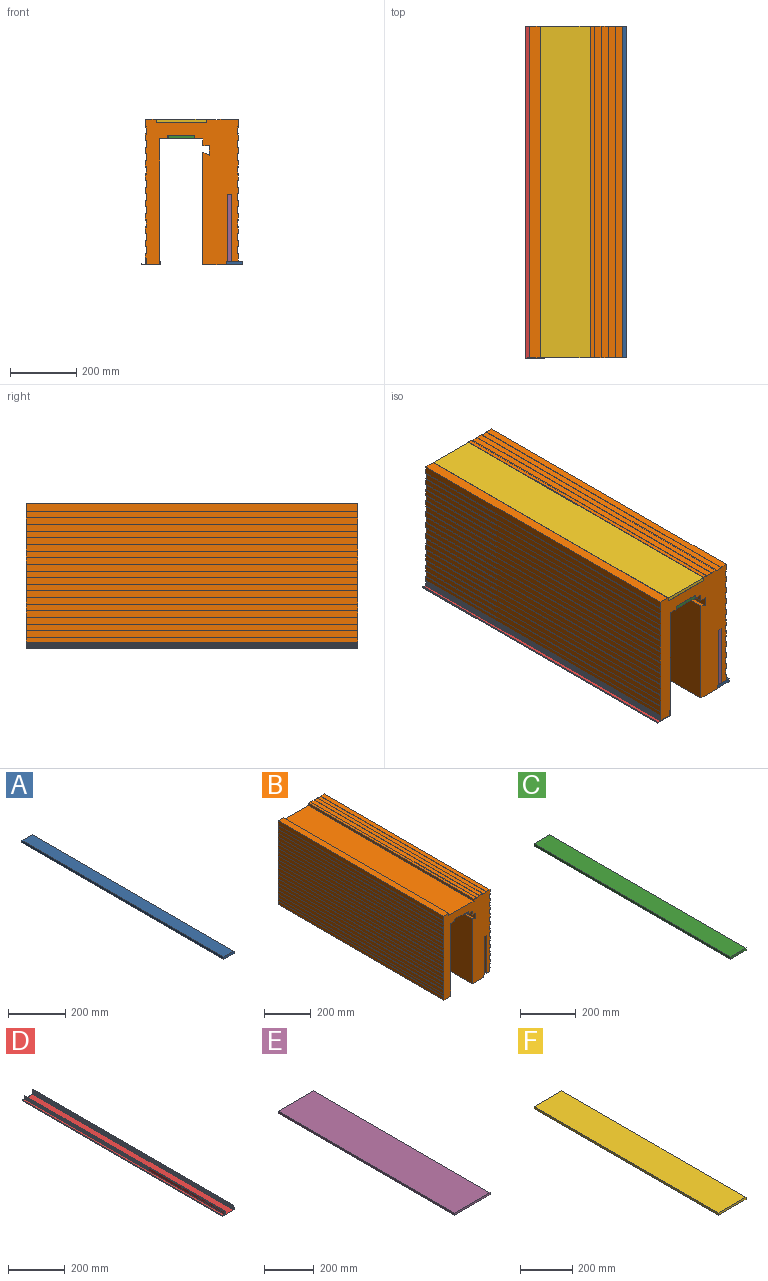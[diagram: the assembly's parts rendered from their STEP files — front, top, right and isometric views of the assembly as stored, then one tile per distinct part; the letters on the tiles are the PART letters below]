
ASSEMBLY  parts=6 mates=5
PART A: 6 faces, bbox 50x1000x10 mm
  f0: plane 1000x10mm, normal (-1,0,0), area 10000mm2, adj f1,f3,f4,f5
  f1: plane 1000x50mm, normal (0,0,-1), area 50000mm2, adj f0,f2,f4,f5
  f2: plane 1000x10mm, normal (1,0,0), area 10000mm2, adj f1,f3,f4,f5
  f3: plane 1000x50mm, normal (0,0,1), area 50000mm2, adj f0,f2,f4,f5
  f4: plane 50x10mm, normal (0,-1,0), area 500mm2, adj f0,f1,f2,f3
  f5: plane 50x10mm, normal (0,1,0), area 500mm2, adj f0,f1,f2,f3
PART B: 120 faces, bbox 280x1000x440 mm
  f0: plane 1000x2mm, normal (0.89,0,-0.45), area 2236.1mm2, adj f1,f117,f118,f119
  f1: plane 1000x20mm, normal (0,0,1), area 20000mm2, adj f0,f2,f118,f119
  f2: plane 1000x2mm, normal (-0.89,0,-0.45), area 2236.1mm2, adj f1,f3,f118,f119
  f3: plane 1000x23mm, normal (0,0,1), area 23000mm2, adj f2,f4,f118,f119
  f4: plane 1000x2mm, normal (0.89,0,-0.45), area 2236.1mm2, adj f3,f5,f118,f119
  f5: plane 1000x13.5mm, normal (0,0,1), area 13500mm2, adj f4,f6,f118,f119
  f6: plane 1000x11.5mm, normal (-1,0,0), area 11500mm2, adj f5,f7,f118,f119
  f7: plane 1000x151mm, normal (0,0,1), area 151000mm2, adj f6,f8,f118,f119
  f8: plane 1000x11.5mm, normal (1,0,0), area 11500mm2, adj f7,f9,f118,f119
  f9: plane 1000x32.4mm, normal (0,0,1), area 32400mm2, adj f8,f10,f118,f119
  f10: plane 1000x25mm, normal (-1,0,0), area 25000mm2, adj f9,f11,f118,f119
  f11: plane 1000x2mm, normal (0.45,0,-0.89), area 2236.1mm2, adj f10,f12,f118,f119
  f12: plane 1000x22mm, normal (-1,0,0), area 22000mm2, adj f11,f13,f118,f119
  f13: plane 1000x2mm, normal (0.45,0,0.89), area 2236.1mm2, adj f12,f14,f118,f119
  f14: plane 1000x20mm, normal (-1,0,0), area 20000mm2, adj f13,f15,f118,f119
  f15: plane 1000x2mm, normal (0.45,0,-0.89), area 2236.1mm2, adj f14,f16,f118,f119
  f16: plane 1000x22mm, normal (-1,0,0), area 22000mm2, adj f15,f17,f118,f119
  f17: plane 1000x2mm, normal (0.45,0,0.89), area 2236.1mm2, adj f16,f18,f118,f119
  f18: plane 1000x20mm, normal (-1,0,0), area 20000mm2, adj f17,f19,f118,f119
  f19: plane 1000x2mm, normal (0.45,0,-0.89), area 2236.1mm2, adj f18,f20,f118,f119
  f20: plane 1000x22mm, normal (-1,0,0), area 22000mm2, adj f19,f21,f118,f119
  f21: plane 1000x2mm, normal (0.45,0,0.89), area 2236.1mm2, adj f20,f22,f118,f119
  f22: plane 1000x20mm, normal (-1,0,0), area 20000mm2, adj f21,f23,f118,f119
  f23: plane 1000x2mm, normal (0.45,0,-0.89), area 2236.1mm2, adj f22,f24,f118,f119
  f24: plane 1000x22mm, normal (-1,0,0), area 22000mm2, adj f23,f25,f118,f119
  f25: plane 1000x2mm, normal (0.45,0,0.89), area 2236.1mm2, adj f24,f26,f118,f119
  f26: plane 1000x20mm, normal (-1,0,0), area 20000mm2, adj f25,f27,f118,f119
  f27: plane 1000x2mm, normal (0.45,0,-0.89), area 2236.1mm2, adj f26,f28,f118,f119
  f28: plane 1000x22mm, normal (-1,0,0), area 22000mm2, adj f27,f29,f118,f119
  f29: plane 1000x2mm, normal (0.45,0,0.89), area 2236.1mm2, adj f28,f30,f118,f119
  f30: plane 1000x20mm, normal (-1,0,0), area 20000mm2, adj f29,f31,f118,f119
  f31: plane 1000x2mm, normal (0.45,0,-0.89), area 2236.1mm2, adj f30,f32,f118,f119
  f32: plane 1000x22mm, normal (-1,0,0), area 22000mm2, adj f31,f33,f118,f119
  f33: plane 1000x2mm, normal (0.45,0,0.89), area 2236.1mm2, adj f32,f34,f118,f119
  f34: plane 1000x20mm, normal (-1,0,0), area 20000mm2, adj f33,f35,f118,f119
  f35: plane 1000x2mm, normal (0.45,0,-0.89), area 2236.1mm2, adj f34,f36,f118,f119
  f36: plane 1000x22mm, normal (-1,0,0), area 22000mm2, adj f35,f37,f118,f119
  f37: plane 1000x2mm, normal (0.45,0,0.89), area 2236.1mm2, adj f36,f38,f118,f119
  f38: plane 1000x20mm, normal (-1,0,0), area 20000mm2, adj f37,f39,f118,f119
  f39: plane 1000x2mm, normal (0.45,0,-0.89), area 2236.1mm2, adj f38,f40,f118,f119
  f40: plane 1000x22mm, normal (-1,0,0), area 22000mm2, adj f39,f41,f118,f119
  f41: plane 1000x2mm, normal (0.45,0,0.89), area 2236.1mm2, adj f40,f42,f118,f119
  f42: plane 1000x20mm, normal (-1,0,0), area 20000mm2, adj f41,f43,f118,f119
  f43: plane 1000x2mm, normal (0.45,0,-0.89), area 2236.1mm2, adj f42,f44,f118,f119
  f44: plane 1000x22mm, normal (-1,0,0), area 22000mm2, adj f43,f45,f118,f119
  f45: plane 1000x2mm, normal (0.45,0,0.89), area 2236.1mm2, adj f44,f46,f118,f119
  f46: plane 1000x20mm, normal (-1,0,0), area 20000mm2, adj f45,f47,f118,f119
  f47: plane 1000x2mm, normal (0.45,0,-0.89), area 2236.1mm2, adj f46,f48,f118,f119
  f48: plane 1000x22mm, normal (-1,0,0), area 22000mm2, adj f47,f49,f118,f119
  f49: plane 1000x2mm, normal (0.45,0,0.89), area 2236.1mm2, adj f48,f50,f118,f119
  f50: plane 1000x15mm, normal (-1,0,0), area 15000mm2, adj f49,f51,f118,f119
  f51: plane 1000x1.9mm, normal (0,0,-1), area 1899.3mm2, adj f50,f52,f118,f119
  f52: plane 1000x18.5mm, normal (-1,0,0), area 18504.2mm2, adj f51,f53,f118,f119
  f53: plane 1000x39.1mm, normal (0,0,-1), area 39100mm2, adj f52,f54,f118,f119
  f54: plane 1000x21.53mm, normal (1,0,0), area 21529.7mm2, adj f53,f55,f118,f119
  f55: plane 1000x1.9mm, normal (0,0,-1), area 1900.7mm2, adj f54,f56,f118,f119
  f56: plane 1000x357mm, normal (1,0,0), area 357000mm2, adj f55,f57,f118,f119
  f57: plane 1000x24.5mm, normal (0,0,-1), area 24500mm2, adj f56,f58,f118,f119
  f58: plane 1000x11.5mm, normal (1,0,0), area 11500mm2, adj f57,f59,f118,f119
  f59: plane 1000x81mm, normal (0,0,-1), area 81000mm2, adj f58,f60,f118,f119
  f60: plane 1000x11.5mm, normal (-1,0,0), area 11500mm2, adj f59,f61,f118,f119
  f61: plane 1000x24.5mm, normal (0,0,-1), area 24500mm2, adj f60,f62,f118,f119
  f62: plane 1000x20mm, normal (-1,0,0), area 20000mm2, adj f61,f63,f118,f119
  f63: plane 1000x20mm, normal (0,0,-1), area 20000mm2, adj f62,f64,f118,f119
  f64: plane 1000x30mm, normal (-1,0,0), area 30000mm2, adj f63,f65,f118,f119
  f65: plane 1000x20mm, normal (0.45,0,0.89), area 22360.7mm2, adj f64,f66,f118,f119
  f66: plane 1000x340mm, normal (-1,0,0), area 340000mm2, adj f65,f67,f118,f119
  f67: plane 1000x70.1mm, normal (0,0,-1), area 70100mm2, adj f66,f68,f118,f119
  f68: plane 1000x11.5mm, normal (1,0,0), area 11500mm2, adj f67,f69,f118,f119
  f69: plane 1000x5mm, normal (0,0,-1), area 5000mm2, adj f68,f70,f118,f119
  f70: plane 1000x201mm, normal (1,0,0), area 201000mm2, adj f69,f71,f118,f119
  f71: plane 1000x10.8mm, normal (0,0,-1), area 10800mm2, adj f70,f72,f118,f119
  f72: plane 1000x201mm, normal (-1,0,0), area 201000mm2, adj f71,f73,f118,f119
  f73: plane 1000x21.2mm, normal (0,0,-1), area 21200mm2, adj f72,f74,f118,f119
  f74: plane 1000x23.5mm, normal (1,0,0), area 23500mm2, adj f73,f75,f118,f119
  f75: plane 1000x2mm, normal (-0.45,0,0.89), area 2236.1mm2, adj f74,f76,f118,f119
  f76: plane 1000x22mm, normal (1,0,0), area 22000mm2, adj f75,f77,f118,f119
  f77: plane 1000x2mm, normal (-0.45,0,-0.89), area 2236.1mm2, adj f76,f78,f118,f119
  f78: plane 1000x20mm, normal (1,0,0), area 20000mm2, adj f77,f79,f118,f119
  f79: plane 1000x2mm, normal (-0.45,0,0.89), area 2236.1mm2, adj f78,f80,f118,f119
  f80: plane 1000x22mm, normal (1,0,0), area 22000mm2, adj f79,f81,f118,f119
  f81: plane 1000x2mm, normal (-0.45,0,-0.89), area 2236.1mm2, adj f80,f82,f118,f119
  f82: plane 1000x20mm, normal (1,0,0), area 20000mm2, adj f81,f83,f118,f119
  f83: plane 1000x2mm, normal (-0.45,0,0.89), area 2236.1mm2, adj f82,f84,f118,f119
  f84: plane 1000x22mm, normal (1,0,0), area 22000mm2, adj f83,f85,f118,f119
  f85: plane 1000x2mm, normal (-0.45,0,-0.89), area 2236.1mm2, adj f84,f86,f118,f119
  f86: plane 1000x20mm, normal (1,0,0), area 20000mm2, adj f85,f87,f118,f119
  f87: plane 1000x2mm, normal (-0.45,0,0.89), area 2236.1mm2, adj f86,f88,f118,f119
  f88: plane 1000x22mm, normal (1,0,0), area 22000mm2, adj f87,f89,f118,f119
  f89: plane 1000x2mm, normal (-0.45,0,-0.89), area 2236.1mm2, adj f88,f90,f118,f119
  f90: plane 1000x20mm, normal (1,0,0), area 20000mm2, adj f89,f91,f118,f119
  f91: plane 1000x2mm, normal (-0.45,0,0.89), area 2236.1mm2, adj f90,f92,f118,f119
  f92: plane 1000x22mm, normal (1,0,0), area 22000mm2, adj f91,f93,f118,f119
  f93: plane 1000x2mm, normal (-0.45,0,-0.89), area 2236.1mm2, adj f92,f94,f118,f119
  f94: plane 1000x20mm, normal (1,0,0), area 20000mm2, adj f93,f95,f118,f119
  f95: plane 1000x2mm, normal (-0.45,0,0.89), area 2236.1mm2, adj f94,f96,f118,f119
  f96: plane 1000x22mm, normal (1,0,0), area 22000mm2, adj f95,f97,f118,f119
  f97: plane 1000x2mm, normal (-0.45,0,-0.89), area 2236.1mm2, adj f96,f98,f118,f119
  f98: plane 1000x20mm, normal (1,0,0), area 20000mm2, adj f97,f99,f118,f119
  f99: plane 1000x2mm, normal (-0.45,0,0.89), area 2236.1mm2, adj f98,f100,f118,f119
  f100: plane 1000x22mm, normal (1,0,0), area 22000mm2, adj f99,f101,f118,f119
  f101: plane 1000x2mm, normal (-0.45,0,-0.89), area 2236.1mm2, adj f100,f102,f118,f119
  f102: plane 1000x20mm, normal (1,0,0), area 20000mm2, adj f101,f103,f118,f119
  f103: plane 1000x2mm, normal (-0.45,0,0.89), area 2236.1mm2, adj f102,f104,f118,f119
  f104: plane 1000x22mm, normal (1,0,0), area 22000mm2, adj f103,f105,f118,f119
  f105: plane 1000x2mm, normal (-0.45,0,-0.89), area 2236.1mm2, adj f104,f106,f118,f119
  f106: plane 1000x20mm, normal (1,0,0), area 20000mm2, adj f105,f107,f118,f119
  f107: plane 1000x2mm, normal (-0.45,0,0.89), area 2236.1mm2, adj f106,f108,f118,f119
  f108: plane 1000x22mm, normal (1,0,0), area 22000mm2, adj f107,f109,f118,f119
  f109: plane 1000x2mm, normal (-0.45,0,-0.89), area 2236.1mm2, adj f108,f110,f118,f119
  f110: plane 1000x20mm, normal (1,0,0), area 20000mm2, adj f109,f111,f118,f119
  f111: plane 1000x2mm, normal (-0.45,0,0.89), area 2236.1mm2, adj f110,f112,f118,f119
  f112: plane 1000x22mm, normal (1,0,0), area 22000mm2, adj f111,f113,f118,f119
  f113: plane 1000x2mm, normal (-0.45,0,-0.89), area 2236.1mm2, adj f112,f114,f118,f119
  f114: plane 1000x25mm, normal (1,0,0), area 25000mm2, adj f113,f115,f118,f119
  f115: plane 1000x22.1mm, normal (0,0,1), area 22100mm2, adj f114,f116,f118,f119
  f116: plane 1000x2mm, normal (-0.89,0,-0.45), area 2236.1mm2, adj f115,f117,f118,f119
  f117: plane 1000x22mm, normal (0,0,1), area 22000mm2, adj f0,f116,f118,f119
  f118: plane 440x280mm, normal (0,-1,0), area 66970mm2, adj f0,f1,f2,f3,f4,f5,f6,f7
  f119: plane 440x280mm, normal (0,1,0), area 66970mm2, adj f0,f1,f2,f3,f4,f5,f6,f7
PART C: 6 faces, bbox 80x1000x10 mm
  f0: plane 1000x10mm, normal (-1,0,0), area 10000mm2, adj f1,f3,f4,f5
  f1: plane 1000x80mm, normal (0,0,-1), area 80000mm2, adj f0,f2,f4,f5
  f2: plane 1000x10mm, normal (1,0,0), area 10000mm2, adj f1,f3,f4,f5
  f3: plane 1000x80mm, normal (0,0,1), area 80000mm2, adj f0,f2,f4,f5
  f4: plane 80x10mm, normal (0,-1,0), area 800mm2, adj f0,f1,f2,f3
  f5: plane 80x10mm, normal (0,1,0), area 800mm2, adj f0,f1,f2,f3
PART D: 62 faces, bbox 57.5x1000x21 mm
  f0: plane 1000x14.3mm, normal (-1,0,0), area 14303.9mm2, adj f1,f2,f60,f61
  f1: plane 57.5x21mm, normal (0,-1,0), area 145.8mm2, adj f0,f2,f3,f4,f5,f6,f7,f8
  f2: plane 1000x11mm, normal (0,0,1), area 11000mm2, adj f0,f1,f3,f60
  f3: plane 1000x1.5mm, normal (1,0,0), area 1500mm2, adj f1,f2,f4,f60
  f4: plane 1000x1.5mm, normal (0,0,1), area 1500mm2, adj f1,f3,f5,f60
  f5: plane 1000x3mm, normal (-1,0,0), area 3000mm2, adj f1,f4,f6,f60
  f6: plane 1000x57.5mm, normal (0,0,-1), area 57500mm2, adj f1,f5,f7,f60
  f7: plane 1000x4mm, normal (1,0,0), area 4000mm2, adj f1,f6,f8,f60
  f8: plane 1000x1mm, normal (0,0,1), area 1000mm2, adj f1,f7,f9,f60
  f9: plane 1000x3mm, normal (-1,0,0), area 3000mm2, adj f1,f8,f10,f60
  f10: plane 1000x1mm, normal (0,0,1), area 1000mm2, adj f1,f9,f11,f60
  f11: plane 1000x7mm, normal (1,0,0), area 7000mm2, adj f1,f10,f12,f60
  f12: plane 1000x1mm, normal (0,0,-1), area 1000mm2, adj f1,f11,f13,f60
  f13: plane 1000x3mm, normal (-1,0,0), area 3000mm2, adj f1,f12,f14,f60
  f14: plane 1000x1mm, normal (0,0,-1), area 1000mm2, adj f1,f13,f15,f60
  f15: plane 1000x4mm, normal (1,0,0), area 4000mm2, adj f1,f14,f16,f60
  f16: plane 1000x2mm, normal (0,0,1), area 2000mm2, adj f1,f15,f17,f60
  f17: plane 1000x12mm, normal (1,0,0), area 12000mm2, adj f1,f16,f18,f60
  f18: plane 1000x1mm, normal (0,0,1), area 1000mm2, adj f1,f17,f19,f60
  f19: plane 1000x1.73mm, normal (-0.87,0,0.5), area 2000mm2, adj f1,f18,f20,f60
  f20: plane 1000x1mm, normal (0,0,-1), area 1000mm2, adj f1,f19,f21,f60
  f21: plane 1000x1.73mm, normal (-0.87,0,0.5), area 2000mm2, adj f1,f20,f22,f60
  f22: plane 1000x1mm, normal (0,0,-1), area 1000mm2, adj f1,f21,f23,f60
  f23: plane 1000x1.73mm, normal (-0.87,0,0.5), area 2000mm2, adj f1,f22,f24,f60
  f24: plane 1000x1mm, normal (0,0,-1), area 1000mm2, adj f1,f23,f25,f60
  f25: plane 1000x1.73mm, normal (-0.87,0,0.5), area 2000mm2, adj f1,f24,f26,f60
  f26: plane 1000x1mm, normal (0,0,-1), area 1000mm2, adj f1,f25,f27,f60
  f27: plane 1000x1.73mm, normal (-0.87,0,0.5), area 2000mm2, adj f1,f26,f28,f60
  f28: plane 1000x1mm, normal (0,0,-1), area 1000mm2, adj f1,f27,f29,f60
  f29: plane 1000x1.73mm, normal (-0.87,0,0.5), area 2000mm2, adj f1,f28,f30,f60
  f30: plane 1000x1mm, normal (0,0,-1), area 1000mm2, adj f1,f29,f31,f60
  f31: plane 1000x1.73mm, normal (-0.87,0,0.5), area 2000mm2, adj f1,f30,f32,f60
  f32: plane 1000x1mm, normal (0,0,-1), area 1000mm2, adj f1,f31,f33,f60
  f33: plane 1000x1.73mm, normal (-0.87,0,0.5), area 2000mm2, adj f1,f32,f34,f60
  f34: plane 1000x1mm, normal (0,0,-1), area 1000mm2, adj f1,f33,f35,f60
  f35: plane 1000x1.73mm, normal (-0.87,0,0.5), area 2000mm2, adj f1,f34,f36,f60
  f36: plane 1000x1mm, normal (0,0,-1), area 1000mm2, adj f1,f35,f37,f60
  f37: plane 1000x1.73mm, normal (-0.87,0,0.5), area 2000mm2, adj f1,f36,f38,f60
  f38: plane 1000x1mm, normal (0,0,-1), area 1000mm2, adj f1,f37,f39,f60
  f39: plane 1000x1.73mm, normal (-0.87,0,0.5), area 2000mm2, adj f1,f38,f40,f60
  f40: plane 1000x1mm, normal (0,0,-1), area 1000mm2, adj f1,f39,f41,f60
  f41: plane 1000x0.45mm, normal (-1,0,0), area 447.4mm2, adj f1,f40,f42,f60
  f42: plane 1000x41mm, normal (0,0,1), area 41000mm2, adj f1,f41,f43,f60
  f43: plane 1000x0.45mm, normal (1,0,0), area 447.4mm2, adj f1,f42,f44,f60
  f44: plane 1000x1mm, normal (0,0,-1), area 1000mm2, adj f1,f43,f45,f60
  f45: plane 1000x1.73mm, normal (0.87,0,0.5), area 2000mm2, adj f1,f44,f46,f60
  f46: plane 1000x1mm, normal (0,0,-1), area 1000mm2, adj f1,f45,f47,f60
  f47: plane 1000x1.73mm, normal (0.87,0,0.5), area 2000mm2, adj f1,f46,f48,f60
  f48: plane 1000x1mm, normal (0,0,-1), area 1000mm2, adj f1,f47,f49,f60
  f49: plane 1000x1.73mm, normal (0.87,0,0.5), area 2000mm2, adj f1,f48,f50,f60
  f50: plane 1000x1mm, normal (0,0,-1), area 1000mm2, adj f1,f49,f51,f60
  f51: plane 1000x1.73mm, normal (0.87,0,0.5), area 2000mm2, adj f1,f50,f52,f60
  f52: plane 1000x1mm, normal (0,0,-1), area 1000mm2, adj f1,f51,f53,f60
  f53: plane 1000x1.73mm, normal (0.87,0,0.5), area 2000mm2, adj f1,f52,f54,f60
  f54: plane 1000x1mm, normal (0,0,-1), area 1000mm2, adj f1,f53,f55,f60
  f55: plane 1000x1.73mm, normal (0.87,0,0.5), area 2000mm2, adj f1,f54,f56,f60
  f56: plane 1000x1mm, normal (0,0,-1), area 1000mm2, adj f1,f55,f57,f60
  f57: plane 1000x1.73mm, normal (0.87,0,0.5), area 2000mm2, adj f1,f56,f58,f60
  f58: plane 1000x1mm, normal (0,0,-1), area 1000mm2, adj f1,f57,f59,f60
  f59: plane 1000x1.73mm, normal (0.87,0,0.5), area 2000mm2, adj f1,f58,f60,f61
  f60: plane 57.5x21mm, normal (0,1,0), area 145.8mm2, adj f0,f2,f3,f4,f5,f6,f7,f8
  f61: plane 1000x1mm, normal (0,0,1), area 1000mm2, adj f0,f1,f59,f60
PART E: 6 faces, bbox 200x1000x10 mm
  f0: plane 1000x10mm, normal (-1,0,0), area 10000mm2, adj f1,f3,f4,f5
  f1: plane 1000x200mm, normal (0,0,-1), area 200000mm2, adj f0,f2,f4,f5
  f2: plane 1000x10mm, normal (1,0,0), area 10000mm2, adj f1,f3,f4,f5
  f3: plane 1000x200mm, normal (0,0,1), area 200000mm2, adj f0,f2,f4,f5
  f4: plane 200x10mm, normal (0,-1,0), area 2000mm2, adj f0,f1,f2,f3
  f5: plane 200x10mm, normal (0,1,0), area 2000mm2, adj f0,f1,f2,f3
PART F: 6 faces, bbox 150x1000x10 mm
  f0: plane 1000x10mm, normal (-1,0,0), area 10000mm2, adj f1,f3,f4,f5
  f1: plane 1000x150mm, normal (0,0,-1), area 150000mm2, adj f0,f2,f4,f5
  f2: plane 1000x10mm, normal (1,0,0), area 10000mm2, adj f1,f3,f4,f5
  f3: plane 1000x150mm, normal (0,0,1), area 150000mm2, adj f0,f2,f4,f5
  f4: plane 150x10mm, normal (0,-1,0), area 1500mm2, adj f0,f1,f2,f3
  f5: plane 150x10mm, normal (0,1,0), area 1500mm2, adj f0,f1,f2,f3
PLACE A t=(-364.39,353.04,-38.56)mm
PLACE B t=(-467.39,353.04,-259.56)mm
PLACE C t=(-539.49,353.04,341.44)mm
PLACE D t=(-562.49,353.04,-39.56)mm
PLACE E rot(axis=(0,1,0),90deg) t=(-358.89,353.04,172.44)mm
PLACE F t=(-574.49,353.04,389.44)mm
MATE fastened E.f4 <-> B.f118  axis (0,-1,0) through (-359.39,-646.96,172.94)mm
MATE fastened C.f4 <-> B.f118  axis (0,-1,0) through (-539.99,-646.96,351.94)mm
MATE fastened F.f4 <-> B.f118  axis (0,-1,0) through (-574.99,-646.96,388.94)mm
MATE fastened D.f1 <-> B.f118  axis (0,-1,0) through (-605.49,-646.96,-38.06)mm
MATE fastened A.f4 <-> B.f118  axis (0,-1,0) through (-364.39,-646.96,-28.06)mm
